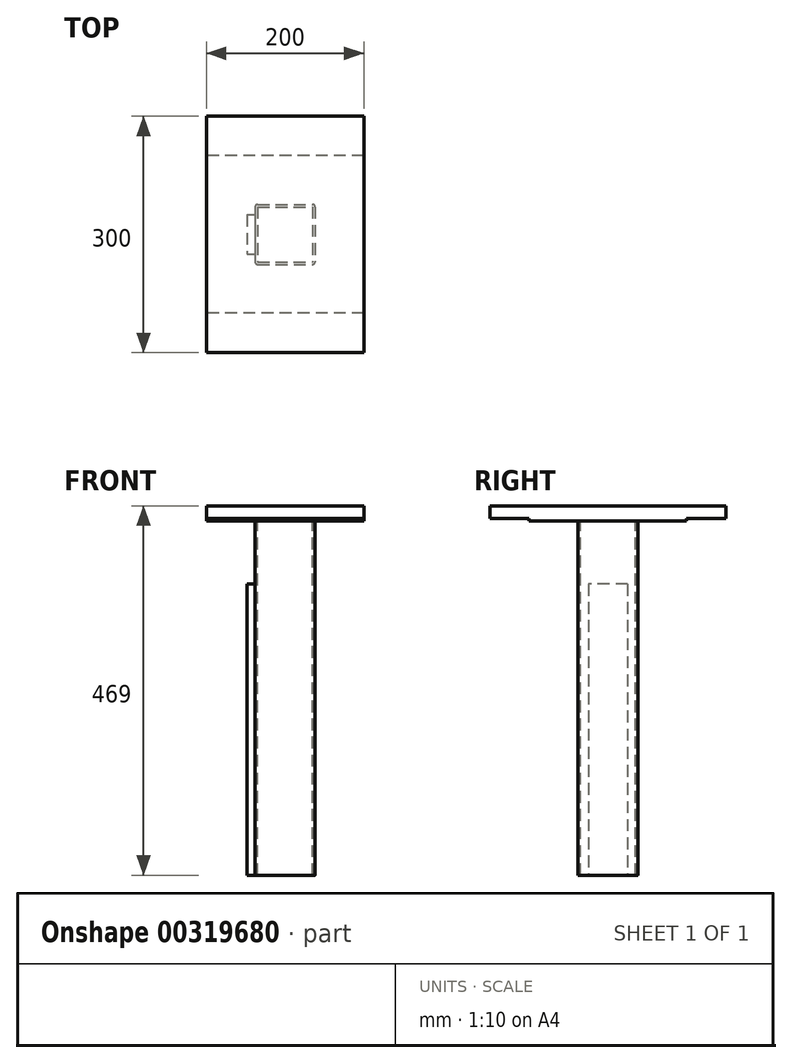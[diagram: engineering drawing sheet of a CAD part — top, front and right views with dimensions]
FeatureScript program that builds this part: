
annotation { "Feature Type Name" : "Feature", "Feature Type Description" : "" }
export const myFeature = defineFeature(function(context is Context, id is Id, definition is map)
    precondition{}
    {
        {
            var Q0;
            Q0=qCreatedBy(makeId("Top.planeOp"),FACE);
            var sketch = newSketch(context, id + "F0", { "sketchPlane" : qUnion([Q0])});
            skLineSegment(sketch, "E0.bottom", {"start": v(-34.92, 38.1) * mm, "end": v(34.92, 38.1) * mm});
            skLineSegment(sketch, "E0.top", {"start": v(-34.93, -38.1) * mm, "end": v(34.92, -38.1) * mm});
            skLineSegment(sketch, "E0.left", {"start": v(-38.1, 34.93) * mm, "end": v(-38.1, -34.93) * mm});
            skLineSegment(sketch, "E0.right", {"start": v(38.1, 34.93) * mm, "end": v(38.1, -34.93) * mm});
            skPoint(sketch, "E1.visualSharp", {"position": v(38.1, 38.1) * mm});
            skArc(sketch, "E1.filletArc", {"start": v(38.1, 34.93) * mm, "mid": v(37.17, 37.17) * mm, "end": v(34.93, 38.1) * mm});
            skPoint(sketch, "E2.visualSharp", {"position": v(38.1, -38.1) * mm});
            skArc(sketch, "E2.filletArc", {"start": v(34.93, -38.1) * mm, "mid": v(37.17, -37.17) * mm, "end": v(38.1, -34.93) * mm});
            skPoint(sketch, "E3.visualSharp", {"position": v(-38.1, -38.1) * mm});
            skArc(sketch, "E3.filletArc", {"start": v(-38.1, -34.93) * mm, "mid": v(-37.17, -37.17) * mm, "end": v(-34.93, -38.1) * mm});
            skPoint(sketch, "E4.visualSharp", {"position": v(-38.1, 38.1) * mm});
            skArc(sketch, "E4.filletArc", {"start": v(-34.92, 38.1) * mm, "mid": v(-37.17, 37.17) * mm, "end": v(-38.1, 34.93) * mm});
            skLineSegment(sketch, "E5.0", {"start": v(-35.05, 35.05) * mm, "end": v(35.05, 35.05) * mm});
            skLineSegment(sketch, "E5.1", {"start": v(-35.05, 35.05) * mm, "end": v(-35.05, -35.05) * mm});
            skLineSegment(sketch, "E5.2", {"start": v(-35.05, -35.05) * mm, "end": v(35.05, -35.05) * mm});
            skLineSegment(sketch, "E5.3", {"start": v(35.05, 35.05) * mm, "end": v(35.05, -35.05) * mm});
            skSolve(sketch);
        }
        {
            var Q0;
            Q0=makeQuery(id+"F0.imprint","IMPRINT",FACE,{"disambiguationData":[TD([[makeQuery(id+"F0.imprint","IMPRINT",EDGE,{"derivedFrom":sQuery(id+"F0.wireOp",EDGE,"E0.bottom")}),-1.0]])]});
            extrude(context, id + "F1", {"entities" : qUnion([Q0]), "oppositeDirection" : true, "depth" : 450 * mm});
        }
        {
            var Q0;
            Q0=makeQuery(id+"F1.opExtrude","SWEPT_FACE",FACE,{"disambiguationData":[OSD([sQuery(id+"F0.wireOp",EDGE,"E0.left")])]});
            var sketch = newSketch(context, id + "F2", { "sketchPlane" : qUnion([Q0])});
            skLineSegment(sketch, "E6.bottom", {"start": v(-25, -80) * mm, "end": v(25, -80) * mm});
            skLineSegment(sketch, "E6.top", {"start": v(-25, -450) * mm, "end": v(25, -450) * mm});
            skLineSegment(sketch, "E6.left", {"start": v(-25, -80) * mm, "end": v(-25, -450) * mm});
            skLineSegment(sketch, "E6.right", {"start": v(25, -80) * mm, "end": v(25, -450) * mm});
            skSolve(sketch);
        }
        {
            var Q0;
            {var subQ0=sQuery(id+"F2.wireOp",EDGE,"E6.bottom");var subQ1=sQuery(id+"F0.wireOp",EDGE,"E0.left");var subQ2=makeQuery(id+"F1.opExtrude","SWEPT_EDGE",EDGE,{"disambiguationData":[OSD([subQ1,sQuery(id+"F0.wireOp",EDGE,"E4.filletArc")])]});var subQ3=makeQuery(id+"F2.imprint","INTERSECT",VERTEX,{"derivedFrom":[subQ2,subQ0]});Q0=makeQuery(id+"F2.imprint","IMPRINT",FACE,{"disambiguationData":[TD([[makeQuery(id+"F2.imprint","IMPRINT",EDGE,{"disambiguationData":[TD([[subQ3,-1.0]])],"derivedFrom":subQ0}),-1.0]])]});}
            extrude(context, id + "F3", {"entities" : qUnion([Q0]), "operationType" : NewBodyOperationType.ADD, "depth" : 10 * mm});
        }
        {
            var Q0;
            Q0=qCreatedBy(makeId("Top.planeOp"),FACE);
            var sketch = newSketch(context, id + "F4", { "sketchPlane" : qUnion([Q0])});
            skLineSegment(sketch, "E7.bottom", {"start": v(100, -150) * mm, "end": v(-100, -150) * mm});
            skLineSegment(sketch, "E7.top", {"start": v(100, 150) * mm, "end": v(-100, 150) * mm});
            skLineSegment(sketch, "E7.left", {"start": v(100, -150) * mm, "end": v(100, 150) * mm});
            skLineSegment(sketch, "E7.right", {"start": v(-100, -150) * mm, "end": v(-100, 150) * mm});
            skSolve(sketch);
        }
        {
            var Q0;
            Q0=makeQuery(id+"F4.imprint","IMPRINT",FACE,{"disambiguationData":[TD([[makeQuery(id+"F4.imprint","IMPRINT",EDGE,{"derivedFrom":sQuery(id+"F4.wireOp",EDGE,"E7.bottom")}),-1.0]])]});
            extrude(context, id + "F5", {"entities" : qUnion([Q0]), "operationType" : NewBodyOperationType.ADD, "depth" : 19 * mm});
        }
        {
            var Q0;
            Q0=makeQuery(id+"F5.opExtrude","SWEPT_FACE",FACE,{"disambiguationData":[OSD([sQuery(id+"F4.wireOp",EDGE,"E7.right")])]});
            var sketch = newSketch(context, id + "F6", { "sketchPlane" : qUnion([Q0])});
            skLineSegment(sketch, "E8.bottom", {"start": v(150, 0) * mm, "end": v(100, 0) * mm});
            skLineSegment(sketch, "E8.top", {"start": v(150, 3) * mm, "end": v(100, 3) * mm});
            skLineSegment(sketch, "E8.left", {"start": v(150, 0) * mm, "end": v(150, 3) * mm});
            skLineSegment(sketch, "E8.right", {"start": v(100, 0) * mm, "end": v(100, 3) * mm});
            skLineSegment(sketch, "E9.bottom", {"start": v(-150, 0) * mm, "end": v(-100, 0) * mm});
            skLineSegment(sketch, "E9.top", {"start": v(-150, 3) * mm, "end": v(-100, 3) * mm});
            skLineSegment(sketch, "E9.left", {"start": v(-150, 0) * mm, "end": v(-150, 3) * mm});
            skLineSegment(sketch, "E9.right", {"start": v(-100, 0) * mm, "end": v(-100, 3) * mm});
            skSolve(sketch);
        }
        {
            var Q0;
            Q0=makeQuery(id+"F6.imprint","IMPRINT",FACE,{"disambiguationData":[TD([[makeQuery(id+"F6.imprint","IMPRINT",EDGE,{"derivedFrom":sQuery(id+"F6.wireOp",EDGE,"E8.bottom")}),-1.0]])]});
            var Q1;
            Q1=makeQuery(id+"F6.imprint","IMPRINT",FACE,{"disambiguationData":[TD([[makeQuery(id+"F6.imprint","IMPRINT",EDGE,{"derivedFrom":sQuery(id+"F6.wireOp",EDGE,"E9.bottom")}),-1.0]])]});
            extrude(context, id + "F7", {"entities" : qUnion([Q0, Q1]), "operationType" : NewBodyOperationType.REMOVE, "oppositeDirection" : true, "depth" : 254 * mm});
        }
    });
